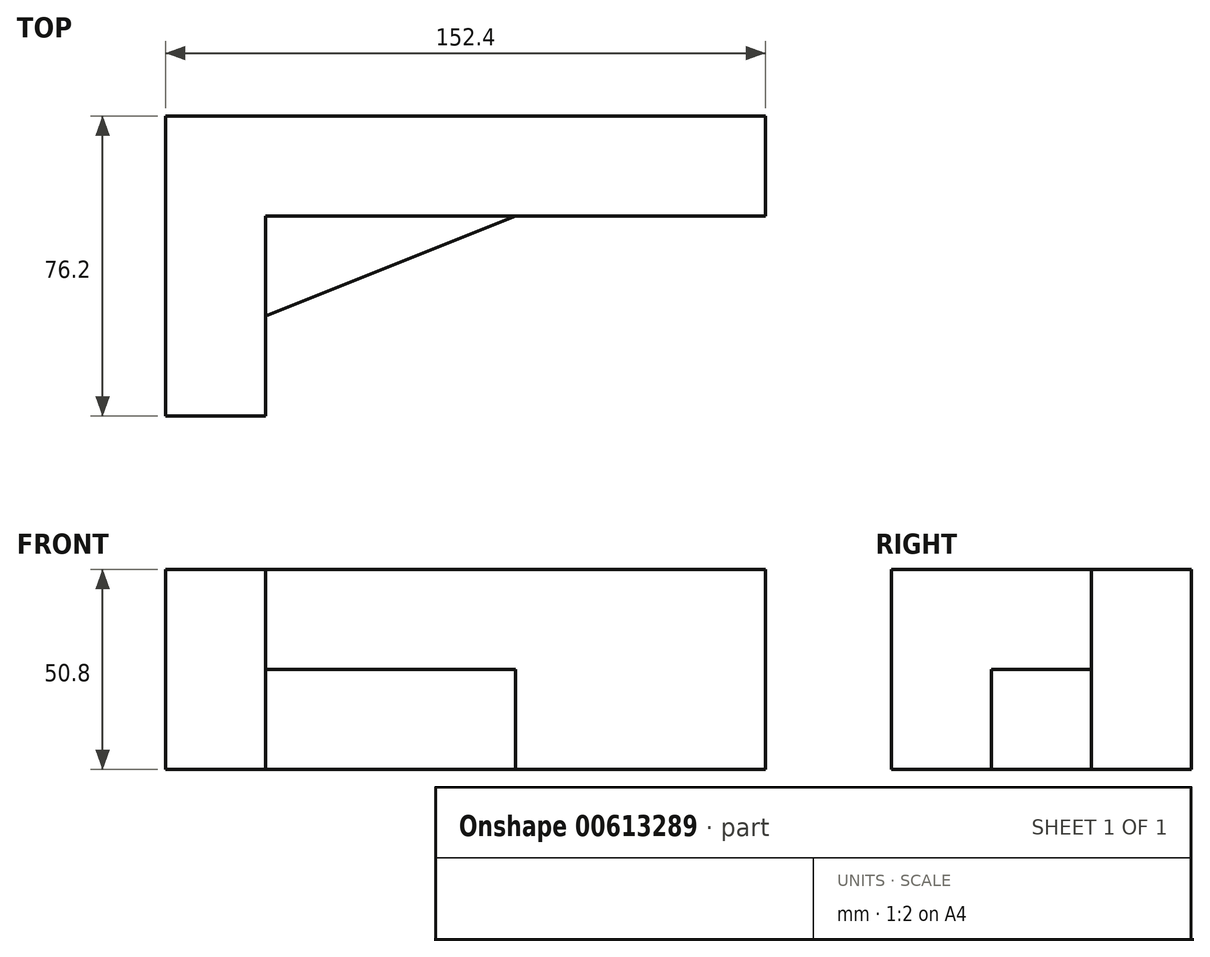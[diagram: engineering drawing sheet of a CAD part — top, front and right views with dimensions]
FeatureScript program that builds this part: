
annotation { "Feature Type Name" : "Feature", "Feature Type Description" : "" }
export const myFeature = defineFeature(function(context is Context, id is Id, definition is map)
    precondition{}
    {
        {
            var Q0;
            Q0=qCreatedBy(makeId("Front.planeOp"),FACE);
            var sketch = newSketch(context, id + "F0", { "sketchPlane" : qUnion([Q0])});
            skLineSegment(sketch, "E0", {"start": v(0, 0) * mm, "end": v(0, 50.8) * mm});
            skLineSegment(sketch, "E1", {"start": v(0, 0) * mm, "end": v(152.4, 0) * mm});
            skLineSegment(sketch, "E2", {"start": v(152.4, 0) * mm, "end": v(152.4, 50.8) * mm});
            skLineSegment(sketch, "E3", {"start": v(152.4, 50.8) * mm, "end": v(0, 50.8) * mm});
            skSolve(sketch);
        }
        {
            var Q0;
            Q0 = qSketchRegion(id + "F0", true);
            extrude(context, id + "F1", {"entities" : qUnion([Q0]), "depth" : 76.2 * mm, "offsetDistance" : 25.4 * mm});
        }
        {
            var Q0;
            Q0=makeQuery(id+"F1.opExtrude","SWEPT_FACE",FACE,{"disambiguationData":[OSD([sQuery(id+"F0.wireOp",EDGE,"E3")])]});
            var sketch = newSketch(context, id + "F2", { "sketchPlane" : qUnion([Q0])});
            skLineSegment(sketch, "E4", {"start": v(0, -76.2) * mm, "end": v(25.4, -76.2) * mm});
            skLineSegment(sketch, "E5", {"start": v(25.4, -76.2) * mm, "end": v(25.4, -25.4) * mm});
            skLineSegment(sketch, "E6", {"start": v(25.4, -25.4) * mm, "end": v(152.4, -25.4) * mm});
            skLineSegment(sketch, "E7", {"start": v(25.4, -50.8) * mm, "end": v(88.9, -25.4) * mm});
            skLineSegment(sketch, "E8", {"start": v(25.4, -50.8) * mm, "end": v(25.4, -25.4) * mm});
            skSolve(sketch);
        }
        {
            var Q0;
            {var subQ6=sQuery(id+"F2.wireOp",EDGE,"E7");Q0=makeQuery(id+"F2.imprint","IMPRINT",FACE,{"disambiguationData":[TD([[makeQuery(id+"F2.imprint","IMPRINT",EDGE,{"derivedFrom":subQ6}),-1.0]])]});}
            extrude(context, id + "F3", {"entities" : qUnion([Q0]), "operationType" : NewBodyOperationType.REMOVE, "oppositeDirection" : true, "depth" : 50.8 * mm, "offsetDistance" : 25.4 * mm});
        }
        {
            var Q0;
            Q0 = qSketchRegion(id + "F2", true);
            extrude(context, id + "F4", {"entities" : qUnion([Q0]), "operationType" : NewBodyOperationType.REMOVE, "oppositeDirection" : true, "depth" : 25.4 * mm, "offsetDistance" : 25.4 * mm});
        }
    });
